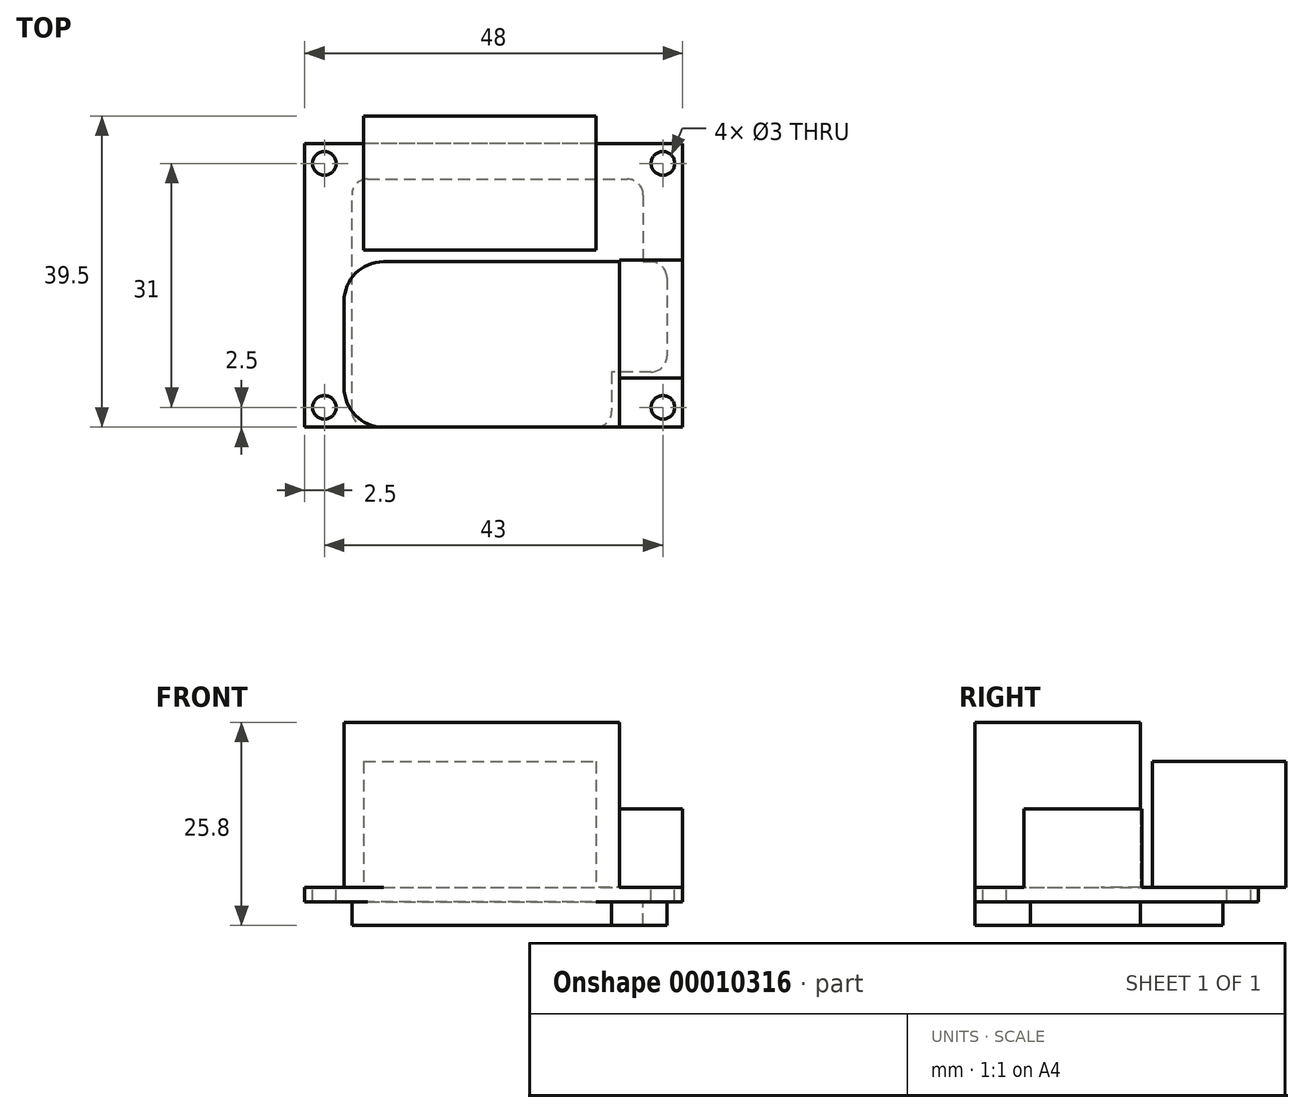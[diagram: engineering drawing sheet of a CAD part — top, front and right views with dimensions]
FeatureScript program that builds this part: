
annotation { "Feature Type Name" : "Feature", "Feature Type Description" : "" }
export const myFeature = defineFeature(function(context is Context, id is Id, definition is map)
    precondition{}
    {
        {
            var Q0;
            Q0=qCreatedBy(makeId("Top.planeOp"),FACE);
            var sketch = newSketch(context, id + "F0", { "sketchPlane" : qUnion([Q0])});
            skLineSegment(sketch, "E0.rect.bottom", {"start": v(24, -18) * mm, "end": v(-24, -18) * mm});
            skLineSegment(sketch, "E0.rect.top", {"start": v(24, 18) * mm, "end": v(-24, 18) * mm});
            skLineSegment(sketch, "E0.rect.left", {"start": v(24, -18) * mm, "end": v(24, 18) * mm});
            skLineSegment(sketch, "E0.rect.right", {"start": v(-24, -18) * mm, "end": v(-24, 18) * mm});
            skPoint(sketch, "E0.rect.middle", {"position": v(0, 0) * mm});
            skSolve(sketch);
        }
        {
            var Q0;
            Q0=makeQuery(id+"F0.imprint","IMPRINT",FACE,{"disambiguationData":[TD([[makeQuery(id+"F0.imprint","IMPRINT",EDGE,{"derivedFrom":sQuery(id+"F0.wireOp",EDGE,"E0.rect.bottom")}),-1.0]])]});
            extrude(context, id + "F1", {"entities" : qUnion([Q0]), "depth" : 1.8 * mm});
        }
        {
            var Q0;
            Q0=makeQuery(id+"F1.opExtrude","CAP_FACE",FACE,{"disambiguationData":[OSD([sQuery(id+"F0.wireOp",EDGE,"E0.rect.bottom"),sQuery(id+"F0.wireOp",EDGE,"E0.rect.top"),sQuery(id+"F0.wireOp",EDGE,"E0.rect.left"),sQuery(id+"F0.wireOp",EDGE,"E0.rect.right")])],"isStart":true});
            var sketch = newSketch(context, id + "F2", { "sketchPlane" : qUnion([Q0])});
            skLineSegment(sketch, "E1", {"start": v(-18, 18) * mm, "end": v(-18, -13.5) * mm});
            skLineSegment(sketch, "E2", {"start": v(-18, -13.5) * mm, "end": v(19, -13.5) * mm});
            skLineSegment(sketch, "E3", {"start": v(19, -13.5) * mm, "end": v(19, -3) * mm});
            skLineSegment(sketch, "E4", {"start": v(19, -3) * mm, "end": v(22, -3) * mm});
            skLineSegment(sketch, "E5", {"start": v(22, -3) * mm, "end": v(22, 11) * mm});
            skLineSegment(sketch, "E6", {"start": v(22, 11) * mm, "end": v(15, 11) * mm});
            skLineSegment(sketch, "E7", {"start": v(15, 11) * mm, "end": v(15, 18) * mm});
            skLineSegment(sketch, "E8", {"start": v(15, 18) * mm, "end": v(-18, 18) * mm});
            skSolve(sketch);
        }
        {
            var Q0;
            Q0=makeQuery(id+"F2.imprint","IMPRINT",FACE,{"disambiguationData":[TD([[makeQuery(id+"F2.imprint","IMPRINT",EDGE,{"derivedFrom":sQuery(id+"F2.wireOp",EDGE,"E1")}),1.0]])]});
            extrude(context, id + "F3", {"entities" : qUnion([Q0]), "operationType" : NewBodyOperationType.ADD, "depth" : 3 * mm});
        }
        {
            var Q0;
            Q0=makeQuery(id+"F1.opExtrude","CAP_FACE",FACE,{"disambiguationData":[OSD([sQuery(id+"F0.wireOp",EDGE,"E0.rect.bottom"),sQuery(id+"F0.wireOp",EDGE,"E0.rect.top"),sQuery(id+"F0.wireOp",EDGE,"E0.rect.left"),sQuery(id+"F0.wireOp",EDGE,"E0.rect.right")])],"isStart":false});
            var sketch = newSketch(context, id + "F4", { "sketchPlane" : qUnion([Q0])});
            skCircle(sketch, "E9", {"center": v(-21.5, 15.5) * mm, "radius": 1.5 * mm});
            skCircle(sketch, "E10", {"center": v(21.5, 15.5) * mm, "radius": 1.5 * mm});
            skCircle(sketch, "E11", {"center": v(21.5, -15.5) * mm, "radius": 1.5 * mm});
            skCircle(sketch, "E12", {"center": v(-21.5, -15.5) * mm, "radius": 1.5 * mm});
            skSolve(sketch);
        }
        {
            var Q0;
            Q0 = qSketchRegion(id + "F4", true);
            extrude(context, id + "F5", {"entities" : qUnion([Q0]), "operationType" : NewBodyOperationType.REMOVE, "endBound" : BoundingType.UP_TO_NEXT, "oppositeDirection" : true, "depth" : 25 * mm});
        }
        {
            var Q0;
            Q0=makeQuery(id+"F1.opExtrude","CAP_FACE",FACE,{"disambiguationData":[OSD([sQuery(id+"F0.wireOp",EDGE,"E0.rect.bottom"),sQuery(id+"F0.wireOp",EDGE,"E0.rect.top"),sQuery(id+"F0.wireOp",EDGE,"E0.rect.left"),sQuery(id+"F0.wireOp",EDGE,"E0.rect.right")])],"isStart":false});
            var sketch = newSketch(context, id + "F6", { "sketchPlane" : qUnion([Q0])});
            skLineSegment(sketch, "E13.bottom", {"start": v(-16.5, 21.5) * mm, "end": v(13, 21.5) * mm});
            skLineSegment(sketch, "E13.top", {"start": v(-16.5, 4.5) * mm, "end": v(13, 4.5) * mm});
            skLineSegment(sketch, "E13.left", {"start": v(-16.5, 21.5) * mm, "end": v(-16.5, 4.5) * mm});
            skLineSegment(sketch, "E13.right", {"start": v(13, 21.5) * mm, "end": v(13, 4.5) * mm});
            skSolve(sketch);
        }
        {
            var Q0;
            Q0 = qSketchRegion(id + "F6", true);
            extrude(context, id + "F7", {"entities" : qUnion([Q0]), "operationType" : NewBodyOperationType.ADD, "depth" : 16 * mm});
        }
        {
            var Q0;
            Q0=makeQuery(id+"F1.opExtrude","CAP_FACE",FACE,{"disambiguationData":[OSD([sQuery(id+"F0.wireOp",EDGE,"E0.rect.bottom"),sQuery(id+"F0.wireOp",EDGE,"E0.rect.top"),sQuery(id+"F0.wireOp",EDGE,"E0.rect.left"),sQuery(id+"F0.wireOp",EDGE,"E0.rect.right")])],"isStart":false});
            var sketch = newSketch(context, id + "F8", { "sketchPlane" : qUnion([Q0])});
            skLineSegment(sketch, "E14.bottom", {"start": v(-19, -18) * mm, "end": v(16, -18) * mm});
            skLineSegment(sketch, "E14.top", {"start": v(-19, 3) * mm, "end": v(16, 3) * mm});
            skLineSegment(sketch, "E14.left", {"start": v(-19, -18) * mm, "end": v(-19, 3) * mm});
            skLineSegment(sketch, "E14.right", {"start": v(16, -18) * mm, "end": v(16, 3) * mm});
            skSolve(sketch);
        }
        {
            var Q0;
            Q0=makeQuery(id+"F8.imprint","IMPRINT",FACE,{"disambiguationData":[TD([[makeQuery(id+"F8.imprint","IMPRINT",EDGE,{"derivedFrom":sQuery(id+"F8.wireOp",EDGE,"E14.bottom")}),-1.0]])]});
            extrude(context, id + "F9", {"entities" : qUnion([Q0]), "operationType" : NewBodyOperationType.ADD, "depth" : 21 * mm});
        }
        {
            var Q0;
            Q0=makeQuery(id+"F9.opExtrude","SWEPT_EDGE",EDGE,{"disambiguationData":[OSD([sQuery(id+"F0.wireOp",EDGE,"E0.rect.bottom"),sQuery(id+"F8.wireOp",EDGE,"E14.bottom"),sQuery(id+"F8.wireOp",EDGE,"E14.left")])]});
            var Q1;
            Q1=makeQuery(id+"F9.opExtrude","SWEPT_EDGE",EDGE,{"disambiguationData":[OSD([sQuery(id+"F8.wireOp",EDGE,"E14.top"),sQuery(id+"F8.wireOp",EDGE,"E14.left")])]});
            fillet(context, id + "F10", {"entities" : qUnion([Q0, Q1]), "radius" : 5 * mm, "tangentPropagation" : true, "allowEdgeOverflow" : false});
        }
        {
            var Q0;
            Q0=makeQuery(id+"F1.opExtrude","CAP_FACE",FACE,{"disambiguationData":[OSD([sQuery(id+"F0.wireOp",EDGE,"E0.rect.bottom"),sQuery(id+"F0.wireOp",EDGE,"E0.rect.top"),sQuery(id+"F0.wireOp",EDGE,"E0.rect.left"),sQuery(id+"F0.wireOp",EDGE,"E0.rect.right")])],"isStart":false});
            var sketch = newSketch(context, id + "F11", { "sketchPlane" : qUnion([Q0])});
            skLineSegment(sketch, "E15.bottom", {"start": v(24, 3.2) * mm, "end": v(16, 3.2) * mm});
            skLineSegment(sketch, "E15.top", {"start": v(24, -11.8) * mm, "end": v(16, -11.8) * mm});
            skLineSegment(sketch, "E15.left", {"start": v(24, 3.2) * mm, "end": v(24, -11.8) * mm});
            skLineSegment(sketch, "E15.right", {"start": v(16, 3.2) * mm, "end": v(16, -11.8) * mm});
            skSolve(sketch);
        }
        {
            var Q0;
            {var subQ2=sQuery(id+"F11.wireOp",EDGE,"E15.bottom");Q0=makeQuery(id+"F11.imprint","IMPRINT",FACE,{"disambiguationData":[TD([[makeQuery(id+"F11.imprint","IMPRINT",EDGE,{"derivedFrom":subQ2}),1.0]])]});}
            extrude(context, id + "F12", {"entities" : qUnion([Q0]), "operationType" : NewBodyOperationType.ADD, "depth" : 10 * mm});
        }
        {
            var Q0;
            Q0=makeQuery(id+"F3.opExtrude","SWEPT_EDGE",EDGE,{"disambiguationData":[OSD([sQuery(id+"F2.wireOp",EDGE,"E2"),sQuery(id+"F2.wireOp",EDGE,"E3")])]});
            var Q1;
            Q1=makeQuery(id+"F3.opExtrude","SWEPT_EDGE",EDGE,{"disambiguationData":[OSD([sQuery(id+"F2.wireOp",EDGE,"E1"),sQuery(id+"F2.wireOp",EDGE,"E2")])]});
            var Q2;
            Q2=makeQuery(id+"F3.opExtrude","SWEPT_EDGE",EDGE,{"disambiguationData":[OSD([sQuery(id+"F0.wireOp",EDGE,"E0.rect.bottom"),sQuery(id+"F2.wireOp",EDGE,"E1"),sQuery(id+"F2.wireOp",EDGE,"E8")])]});
            var Q3;
            Q3=makeQuery(id+"F3.opExtrude","SWEPT_EDGE",EDGE,{"disambiguationData":[OSD([sQuery(id+"F0.wireOp",EDGE,"E0.rect.bottom"),sQuery(id+"F2.wireOp",EDGE,"E7"),sQuery(id+"F2.wireOp",EDGE,"E8")])]});
            var Q4;
            Q4=makeQuery(id+"F3.opExtrude","SWEPT_EDGE",EDGE,{"disambiguationData":[OSD([sQuery(id+"F2.wireOp",EDGE,"E5"),sQuery(id+"F2.wireOp",EDGE,"E6")])]});
            var Q5;
            Q5=makeQuery(id+"F3.opExtrude","SWEPT_EDGE",EDGE,{"disambiguationData":[OSD([sQuery(id+"F2.wireOp",EDGE,"E4"),sQuery(id+"F2.wireOp",EDGE,"E5")])]});
            fillet(context, id + "F13", {"entities" : qUnion([Q0, Q1, Q2, Q3, Q4, Q5]), "radius" : 2 * mm, "tangentPropagation" : true, "allowEdgeOverflow" : false});
        }
    });
